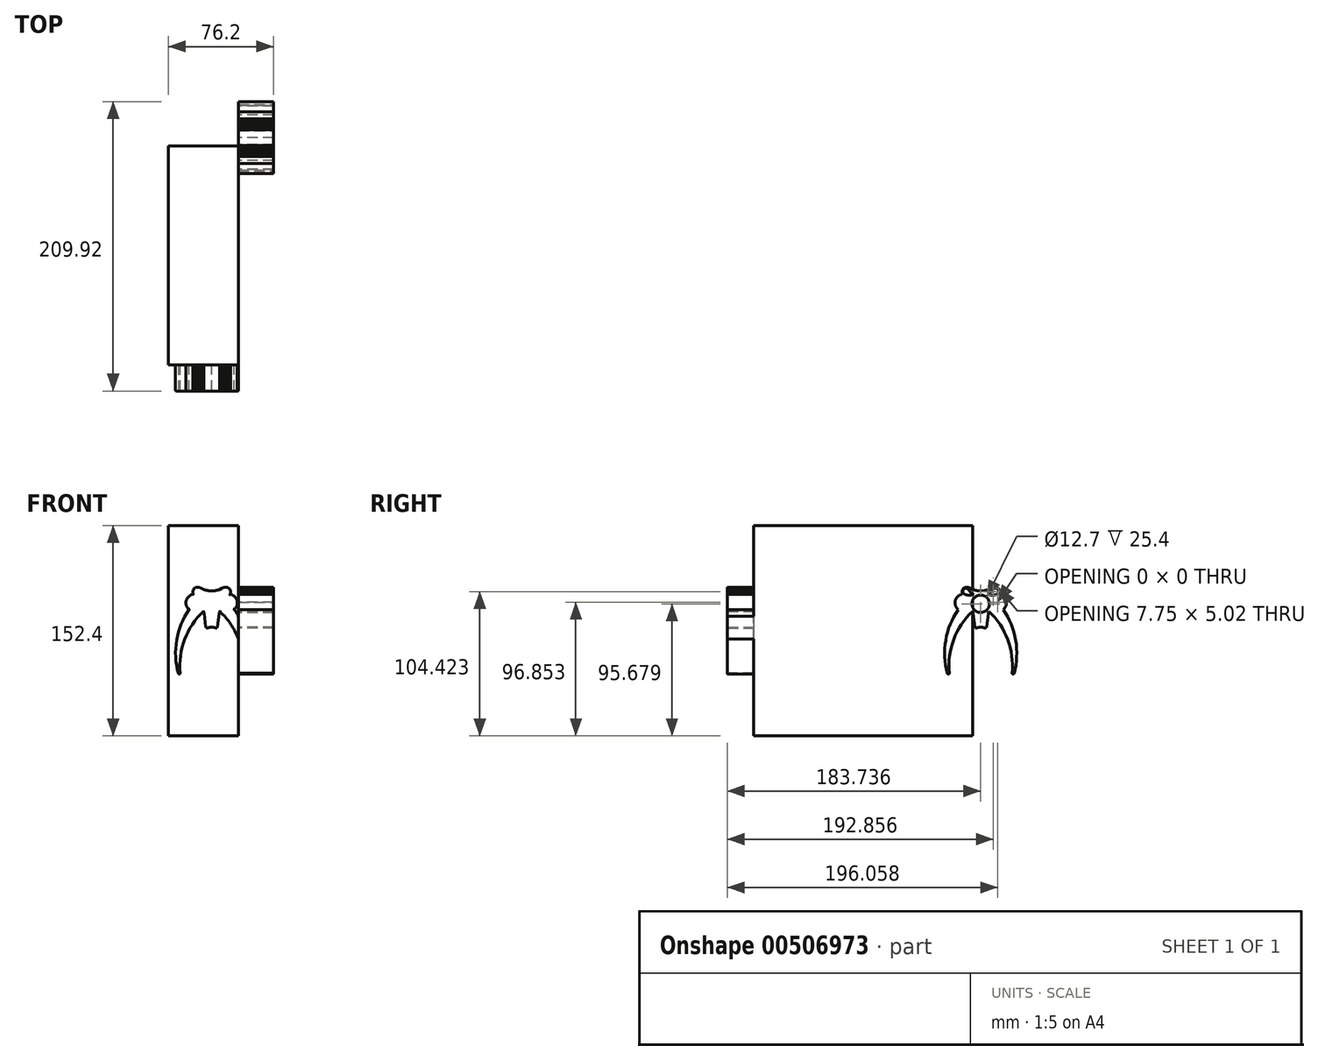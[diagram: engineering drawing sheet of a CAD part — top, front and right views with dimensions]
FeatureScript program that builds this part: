
annotation { "Feature Type Name" : "Feature", "Feature Type Description" : "" }
export const myFeature = defineFeature(function(context is Context, id is Id, definition is map)
    precondition{}
    {
        {
            var Q0;
            Q0=qCreatedBy(makeId("Front.planeOp"),FACE);
            var sketch = newSketch(context, id + "F0", { "sketchPlane" : qUnion([Q0])});
            skLineSegment(sketch, "E0.bottom", {"start": v(-25.4, 76.2) * mm, "end": v(25.4, 76.2) * mm});
            skLineSegment(sketch, "E0.top", {"start": v(-25.4, -76.2) * mm, "end": v(25.4, -76.2) * mm});
            skLineSegment(sketch, "E0.left", {"start": v(-25.4, 76.2) * mm, "end": v(-25.4, -76.2) * mm});
            skLineSegment(sketch, "E0.right", {"start": v(25.4, 76.2) * mm, "end": v(25.4, -76.2) * mm});
            skPoint(sketch, "E0.middle", {"position": v(0, 0) * mm});
            skSolve(sketch);
        }
        {
            var Q0;
            Q0 = qSketchRegion(id + "F0", true);
            extrude(context, id + "F1", {"entities" : qUnion([Q0]), "offsetDistance" : 25.4 * mm, "depth" : 152.4 * mm});
        }
        {
            var Q0;
            Q0=makeQuery(id+"F1.opExtrude","SWEPT_FACE",FACE,{"disambiguationData":[OSD([sQuery(id+"F0.wireOp",EDGE,"E0.right")])]});
            var sketch = newSketch(context, id + "F2", { "sketchPlane" : qUnion([Q0])});
            skArc(sketch, "E1", {"start": v(8.8, 2.02) * mm, "mid": v(7.41, 2.36) * mm, "end": v(5.98, 2.5) * mm});
            skLineSegment(sketch, "E2", {"start": v(11.41, 12.4) * mm, "end": v(10.25, 2.94) * mm});
            skArc(sketch, "E3", {"start": v(8.8, 2.02) * mm, "mid": v(9.74, 2.14) * mm, "end": v(10.25, 2.94) * mm});
            skArc(sketch, "E4", {"start": v(8.18, 0.06) * mm, "mid": v(10.85, 0.4) * mm, "end": v(12.3, 2.67) * mm});
            skLineSegment(sketch, "E5", {"start": v(18.57, 22.34) * mm, "end": v(19.23, 25.45) * mm});
            skLineSegment(sketch, "E6", {"start": v(19.23, 25.45) * mm, "end": v(19.56, 27.12) * mm});
            skLineSegment(sketch, "E7", {"start": v(19.56, 27.12) * mm, "end": v(19.56, 28.58) * mm});
            skLineSegment(sketch, "E8", {"start": v(19.56, 28.58) * mm, "end": v(19.23, 29.78) * mm});
            skLineSegment(sketch, "E9", {"start": v(19.23, 29.78) * mm, "end": v(18.57, 30.68) * mm});
            skLineSegment(sketch, "E10", {"start": v(18.57, 30.68) * mm, "end": v(17.62, 31.25) * mm});
            skLineSegment(sketch, "E11", {"start": v(17.62, 31.25) * mm, "end": v(16.4, 31.45) * mm});
            skLineSegment(sketch, "E12", {"start": v(16.4, 31.45) * mm, "end": v(14.98, 31.3) * mm});
            skLineSegment(sketch, "E13", {"start": v(14.98, 31.3) * mm, "end": v(13.39, 30.77) * mm});
            skLineSegment(sketch, "E14", {"start": v(13.39, 30.77) * mm, "end": v(11.7, 29.9) * mm});
            skArc(sketch, "E15", {"start": v(8.18, 0.06) * mm, "mid": v(7.1, 0.36) * mm, "end": v(5.98, 0.46) * mm});
            skArc(sketch, "E16", {"start": v(5.98, 28.72) * mm, "mid": v(8.9, 29.02) * mm, "end": v(11.7, 29.9) * mm});
            skArc(sketch, "E17", {"start": v(5.98, 28.15) * mm, "mid": v(8.97, 28.6) * mm, "end": v(11.7, 29.9) * mm});
            skArc(sketch, "E18", {"start": v(17.63, 26.41) * mm, "mid": v(18.5, 29.86) * mm, "end": v(14.95, 29.86) * mm});
            skArc(sketch, "E19", {"start": v(11.18, 26.35) * mm, "mid": v(13.29, 27.87) * mm, "end": v(14.95, 29.86) * mm});
            skArc(sketch, "E20", {"start": v(11.18, 26.35) * mm, "mid": v(14.41, 25.71) * mm, "end": v(17.63, 26.41) * mm});
            skCircle(sketch, "E21", {"center": v(8.44, 22.07) * mm, "radius": 0.52 * mm});
            skArc(sketch, "E22", {"start": v(5.98, 16.54) * mm, "mid": v(12.45, 17.6) * mm, "end": v(18.26, 20.65) * mm});
            skLineSegment(sketch, "E23", {"start": v(18.26, 20.65) * mm, "end": v(12.24, 14.18) * mm});
            skArc(sketch, "E24", {"start": v(12.24, 14.18) * mm, "mid": v(11.69, 13.36) * mm, "end": v(11.41, 12.4) * mm});
            skLineSegment(sketch, "E25", {"start": v(12.99, 8.32) * mm, "end": v(12.3, 2.69) * mm});
            skLineSegment(sketch, "E26", {"start": v(20.88, 14.44) * mm, "end": v(17.85, 13.73) * mm});
            skArc(sketch, "E27", {"start": v(20.88, 14.44) * mm, "mid": v(21.65, 14.84) * mm, "end": v(22.36, 15.36) * mm});
            skArc(sketch, "E28", {"start": v(17.85, 13.73) * mm, "mid": v(15.85, 12.88) * mm, "end": v(14.25, 11.4) * mm});
            skArc(sketch, "E29", {"start": v(5.98, 2.5) * mm, "mid": v(4.55, 2.36) * mm, "end": v(3.16, 2.02) * mm});
            skLineSegment(sketch, "E30", {"start": v(0.55, 12.4) * mm, "end": v(1.72, 2.94) * mm});
            skArc(sketch, "E31", {"start": v(1.72, 2.94) * mm, "mid": v(2.22, 2.14) * mm, "end": v(3.16, 2.02) * mm});
            skArc(sketch, "E32", {"start": v(-0.33, 2.67) * mm, "mid": v(1.11, 0.4) * mm, "end": v(3.78, 0.06) * mm});
            skLineSegment(sketch, "E33", {"start": v(0.27, 29.9) * mm, "end": v(-1.42, 30.77) * mm});
            skLineSegment(sketch, "E34", {"start": v(-1.42, 30.77) * mm, "end": v(-3.01, 31.3) * mm});
            skLineSegment(sketch, "E35", {"start": v(-3.01, 31.3) * mm, "end": v(-4.44, 31.45) * mm});
            skLineSegment(sketch, "E36", {"start": v(-4.44, 31.45) * mm, "end": v(-5.66, 31.25) * mm});
            skLineSegment(sketch, "E37", {"start": v(-5.66, 31.25) * mm, "end": v(-6.61, 30.68) * mm});
            skLineSegment(sketch, "E38", {"start": v(-6.61, 30.68) * mm, "end": v(-7.27, 29.78) * mm});
            skLineSegment(sketch, "E39", {"start": v(-7.27, 29.78) * mm, "end": v(-7.6, 28.58) * mm});
            skLineSegment(sketch, "E40", {"start": v(-7.6, 28.58) * mm, "end": v(-7.6, 27.12) * mm});
            skLineSegment(sketch, "E41", {"start": v(-7.6, 27.12) * mm, "end": v(-7.26, 25.45) * mm});
            skLineSegment(sketch, "E42", {"start": v(-7.26, 25.45) * mm, "end": v(-6.6, 22.34) * mm});
            skArc(sketch, "E43", {"start": v(5.98, 0.46) * mm, "mid": v(4.86, 0.36) * mm, "end": v(3.78, 0.06) * mm});
            skArc(sketch, "E44", {"start": v(0.27, 29.9) * mm, "mid": v(3.06, 29.02) * mm, "end": v(5.98, 28.72) * mm});
            skArc(sketch, "E45", {"start": v(0.27, 29.9) * mm, "mid": v(3, 28.6) * mm, "end": v(5.98, 28.15) * mm});
            skArc(sketch, "E46", {"start": v(-2.98, 29.86) * mm, "mid": v(-6.54, 29.86) * mm, "end": v(-5.67, 26.41) * mm});
            skArc(sketch, "E47", {"start": v(-2.98, 29.86) * mm, "mid": v(-1.32, 27.87) * mm, "end": v(0.78, 26.35) * mm});
            skArc(sketch, "E48", {"start": v(-3.55, 30.13) * mm, "mid": v(-4.98, 28.59) * mm, "end": v(-5.56, 26.57) * mm});
            skArc(sketch, "E49", {"start": v(-5.56, 26.57) * mm, "mid": v(-4.13, 28.11) * mm, "end": v(-3.55, 30.13) * mm});
            skArc(sketch, "E50", {"start": v(-5.67, 26.41) * mm, "mid": v(-2.45, 25.71) * mm, "end": v(0.78, 26.35) * mm});
            skCircle(sketch, "E51", {"center": v(3.52, 22.07) * mm, "radius": 0.52 * mm});
            skArc(sketch, "E52", {"start": v(-6.3, 20.65) * mm, "mid": v(-0.5, 17.6) * mm, "end": v(5.98, 16.54) * mm});
            skLineSegment(sketch, "E53", {"start": v(-6.3, 20.65) * mm, "end": v(-0.28, 14.18) * mm});
            skArc(sketch, "E54", {"start": v(0.55, 12.4) * mm, "mid": v(0.28, 13.36) * mm, "end": v(-0.28, 14.18) * mm});
            skLineSegment(sketch, "E55", {"start": v(-1.02, 8.32) * mm, "end": v(-0.33, 2.69) * mm});
            skArc(sketch, "E56", {"start": v(17.52, 26.57) * mm, "mid": v(16.94, 28.59) * mm, "end": v(15.51, 30.13) * mm});
            skArc(sketch, "E57", {"start": v(15.51, 30.13) * mm, "mid": v(16.1, 28.11) * mm, "end": v(17.52, 26.57) * mm});
            skArc(sketch, "E58", {"start": v(14.25, 11.4) * mm, "mid": v(13.41, 9.95) * mm, "end": v(12.99, 8.32) * mm});
            skArc(sketch, "E59", {"start": v(22.36, 15.36) * mm, "mid": v(24.4, 21.81) * mm, "end": v(19.4, 26.38) * mm});
            skLineSegment(sketch, "E60", {"start": v(-8.91, 14.44) * mm, "end": v(-5.89, 13.73) * mm});
            skArc(sketch, "E61", {"start": v(-10.4, 15.36) * mm, "mid": v(-9.68, 14.84) * mm, "end": v(-8.91, 14.44) * mm});
            skArc(sketch, "E62", {"start": v(-2.28, 11.4) * mm, "mid": v(-3.88, 12.88) * mm, "end": v(-5.89, 13.73) * mm});
            skArc(sketch, "E63", {"start": v(-1.02, 8.32) * mm, "mid": v(-1.45, 9.95) * mm, "end": v(-2.28, 11.4) * mm});
            skArc(sketch, "E64", {"start": v(-7.44, 26.38) * mm, "mid": v(-12.44, 21.81) * mm, "end": v(-10.4, 15.36) * mm});
            skCircle(sketch, "E65", {"center": v(5.94, 19.48) * mm, "radius": 3.97 * mm});
            skCircle(sketch, "E66", {"center": v(5.94, 19.48) * mm, "radius": 6.35 * mm});
            skArc(sketch, "E67", {"start": v(28.74, -30.74) * mm, "mid": v(24.77, -4.45) * mm, "end": v(8.67, 16.72) * mm});
            skArc(sketch, "E68", {"start": v(30.16, -30.97) * mm, "mid": v(30.68, -3.66) * mm, "end": v(18.26, 20.65) * mm});
            skArc(sketch, "E69", {"start": v(3.3, 16.72) * mm, "mid": v(-12.8, -4.45) * mm, "end": v(-16.78, -30.74) * mm});
            skArc(sketch, "E70", {"start": v(-6.3, 20.65) * mm, "mid": v(-18.72, -3.66) * mm, "end": v(-18.2, -30.97) * mm});
            skArc(sketch, "E71", {"start": v(28.74, -30.74) * mm, "mid": v(28.91, -31.24) * mm, "end": v(29.4, -31.44) * mm});
            skArc(sketch, "E72", {"start": v(29.4, -31.44) * mm, "mid": v(29.88, -31.35) * mm, "end": v(30.16, -30.97) * mm});
            skArc(sketch, "E73", {"start": v(-17.44, -31.44) * mm, "mid": v(-16.95, -31.24) * mm, "end": v(-16.78, -30.74) * mm});
            skArc(sketch, "E74", {"start": v(-18.2, -30.97) * mm, "mid": v(-17.91, -31.35) * mm, "end": v(-17.44, -31.44) * mm});
            skSolve(sketch);
        }
        {
            var Q0;
            Q0=makeQuery(id+"F1.opExtrude","CAP_FACE",FACE,{"disambiguationData":[OSD([sQuery(id+"F0.wireOp",EDGE,"E0.bottom"),sQuery(id+"F0.wireOp",EDGE,"E0.top"),sQuery(id+"F0.wireOp",EDGE,"E0.left"),sQuery(id+"F0.wireOp",EDGE,"E0.right")])],"isStart":false});
            var sketch = newSketch(context, id + "F3", { "sketchPlane" : qUnion([Q0])});
            skArc(sketch, "E75", {"start": v(8.8, 2.02) * mm, "mid": v(7.41, 2.36) * mm, "end": v(5.98, 2.5) * mm});
            skLineSegment(sketch, "E76", {"start": v(11.41, 12.4) * mm, "end": v(10.25, 2.94) * mm});
            skArc(sketch, "E77", {"start": v(8.8, 2.02) * mm, "mid": v(9.74, 2.14) * mm, "end": v(10.25, 2.94) * mm});
            skArc(sketch, "E78", {"start": v(8.18, 0.06) * mm, "mid": v(10.85, 0.4) * mm, "end": v(12.3, 2.67) * mm});
            skLineSegment(sketch, "E79", {"start": v(18.57, 22.34) * mm, "end": v(19.23, 25.45) * mm});
            skLineSegment(sketch, "E80", {"start": v(19.23, 25.45) * mm, "end": v(19.56, 27.12) * mm});
            skLineSegment(sketch, "E81", {"start": v(19.56, 27.12) * mm, "end": v(19.56, 28.58) * mm});
            skLineSegment(sketch, "E82", {"start": v(19.56, 28.58) * mm, "end": v(19.23, 29.78) * mm});
            skLineSegment(sketch, "E83", {"start": v(19.23, 29.78) * mm, "end": v(18.57, 30.68) * mm});
            skLineSegment(sketch, "E84", {"start": v(18.57, 30.68) * mm, "end": v(17.62, 31.25) * mm});
            skLineSegment(sketch, "E85", {"start": v(17.62, 31.25) * mm, "end": v(16.4, 31.45) * mm});
            skLineSegment(sketch, "E86", {"start": v(16.4, 31.45) * mm, "end": v(14.98, 31.3) * mm});
            skLineSegment(sketch, "E87", {"start": v(14.98, 31.3) * mm, "end": v(13.39, 30.77) * mm});
            skLineSegment(sketch, "E88", {"start": v(13.39, 30.77) * mm, "end": v(11.7, 29.9) * mm});
            skArc(sketch, "E89", {"start": v(8.18, 0.06) * mm, "mid": v(7.1, 0.36) * mm, "end": v(5.98, 0.46) * mm});
            skArc(sketch, "E90", {"start": v(5.98, 28.72) * mm, "mid": v(8.9, 29.02) * mm, "end": v(11.7, 29.9) * mm});
            skArc(sketch, "E91", {"start": v(5.98, 28.15) * mm, "mid": v(8.97, 28.6) * mm, "end": v(11.7, 29.9) * mm});
            skArc(sketch, "E92", {"start": v(17.63, 26.41) * mm, "mid": v(18.5, 29.86) * mm, "end": v(14.95, 29.86) * mm});
            skArc(sketch, "E93", {"start": v(11.18, 26.35) * mm, "mid": v(13.29, 27.87) * mm, "end": v(14.95, 29.86) * mm});
            skArc(sketch, "E94", {"start": v(11.18, 26.35) * mm, "mid": v(14.41, 25.71) * mm, "end": v(17.63, 26.41) * mm});
            skCircle(sketch, "E95", {"center": v(8.44, 22.07) * mm, "radius": 0.52 * mm});
            skArc(sketch, "E96", {"start": v(5.98, 16.54) * mm, "mid": v(12.45, 17.6) * mm, "end": v(18.26, 20.65) * mm});
            skLineSegment(sketch, "E97", {"start": v(18.26, 20.65) * mm, "end": v(12.24, 14.18) * mm});
            skArc(sketch, "E98", {"start": v(12.24, 14.18) * mm, "mid": v(11.69, 13.36) * mm, "end": v(11.41, 12.4) * mm});
            skLineSegment(sketch, "E99", {"start": v(12.99, 8.32) * mm, "end": v(12.3, 2.69) * mm});
            skLineSegment(sketch, "E100", {"start": v(20.88, 14.44) * mm, "end": v(17.85, 13.73) * mm});
            skArc(sketch, "E101", {"start": v(20.88, 14.44) * mm, "mid": v(21.65, 14.84) * mm, "end": v(22.36, 15.36) * mm});
            skArc(sketch, "E102", {"start": v(17.85, 13.73) * mm, "mid": v(15.85, 12.88) * mm, "end": v(14.25, 11.4) * mm});
            skArc(sketch, "E103", {"start": v(5.98, 2.5) * mm, "mid": v(4.55, 2.36) * mm, "end": v(3.16, 2.02) * mm});
            skLineSegment(sketch, "E104", {"start": v(0.55, 12.4) * mm, "end": v(1.72, 2.94) * mm});
            skArc(sketch, "E105", {"start": v(1.72, 2.94) * mm, "mid": v(2.22, 2.14) * mm, "end": v(3.16, 2.02) * mm});
            skArc(sketch, "E106", {"start": v(-0.33, 2.67) * mm, "mid": v(1.11, 0.4) * mm, "end": v(3.78, 0.06) * mm});
            skLineSegment(sketch, "E107", {"start": v(0.27, 29.9) * mm, "end": v(-1.42, 30.77) * mm});
            skLineSegment(sketch, "E108", {"start": v(-1.42, 30.77) * mm, "end": v(-3.01, 31.3) * mm});
            skLineSegment(sketch, "E109", {"start": v(-3.01, 31.3) * mm, "end": v(-4.44, 31.45) * mm});
            skLineSegment(sketch, "E110", {"start": v(-4.44, 31.45) * mm, "end": v(-5.66, 31.25) * mm});
            skLineSegment(sketch, "E111", {"start": v(-5.66, 31.25) * mm, "end": v(-6.61, 30.68) * mm});
            skLineSegment(sketch, "E112", {"start": v(-6.61, 30.68) * mm, "end": v(-7.27, 29.78) * mm});
            skLineSegment(sketch, "E113", {"start": v(-7.27, 29.78) * mm, "end": v(-7.6, 28.58) * mm});
            skLineSegment(sketch, "E114", {"start": v(-7.6, 28.58) * mm, "end": v(-7.6, 27.12) * mm});
            skLineSegment(sketch, "E115", {"start": v(-7.6, 27.12) * mm, "end": v(-7.26, 25.45) * mm});
            skLineSegment(sketch, "E116", {"start": v(-7.26, 25.45) * mm, "end": v(-6.6, 22.34) * mm});
            skArc(sketch, "E117", {"start": v(5.98, 0.46) * mm, "mid": v(4.86, 0.36) * mm, "end": v(3.78, 0.06) * mm});
            skArc(sketch, "E118", {"start": v(0.27, 29.9) * mm, "mid": v(3.06, 29.02) * mm, "end": v(5.98, 28.72) * mm});
            skArc(sketch, "E119", {"start": v(0.27, 29.9) * mm, "mid": v(3, 28.6) * mm, "end": v(5.98, 28.15) * mm});
            skArc(sketch, "E120", {"start": v(-2.98, 29.86) * mm, "mid": v(-6.54, 29.86) * mm, "end": v(-5.67, 26.41) * mm});
            skArc(sketch, "E121", {"start": v(-2.98, 29.86) * mm, "mid": v(-1.32, 27.87) * mm, "end": v(0.78, 26.35) * mm});
            skArc(sketch, "E122", {"start": v(-3.55, 30.13) * mm, "mid": v(-4.98, 28.59) * mm, "end": v(-5.56, 26.57) * mm});
            skArc(sketch, "E123", {"start": v(-5.56, 26.57) * mm, "mid": v(-4.13, 28.11) * mm, "end": v(-3.55, 30.13) * mm});
            skArc(sketch, "E124", {"start": v(-5.67, 26.41) * mm, "mid": v(-2.45, 25.71) * mm, "end": v(0.78, 26.35) * mm});
            skCircle(sketch, "E125", {"center": v(3.52, 22.07) * mm, "radius": 0.52 * mm});
            skArc(sketch, "E126", {"start": v(-6.3, 20.65) * mm, "mid": v(-0.5, 17.6) * mm, "end": v(5.98, 16.54) * mm});
            skLineSegment(sketch, "E127", {"start": v(-6.3, 20.65) * mm, "end": v(-0.28, 14.18) * mm});
            skArc(sketch, "E128", {"start": v(0.55, 12.4) * mm, "mid": v(0.28, 13.36) * mm, "end": v(-0.28, 14.18) * mm});
            skLineSegment(sketch, "E129", {"start": v(-1.02, 8.32) * mm, "end": v(-0.33, 2.69) * mm});
            skArc(sketch, "E130", {"start": v(17.52, 26.57) * mm, "mid": v(16.94, 28.59) * mm, "end": v(15.51, 30.13) * mm});
            skArc(sketch, "E131", {"start": v(15.51, 30.13) * mm, "mid": v(16.1, 28.11) * mm, "end": v(17.52, 26.57) * mm});
            skArc(sketch, "E132", {"start": v(14.25, 11.4) * mm, "mid": v(13.41, 9.95) * mm, "end": v(12.99, 8.32) * mm});
            skArc(sketch, "E133", {"start": v(22.36, 15.36) * mm, "mid": v(24.4, 21.81) * mm, "end": v(19.4, 26.38) * mm});
            skLineSegment(sketch, "E134", {"start": v(-8.91, 14.44) * mm, "end": v(-5.89, 13.73) * mm});
            skArc(sketch, "E135", {"start": v(-10.4, 15.36) * mm, "mid": v(-9.68, 14.84) * mm, "end": v(-8.91, 14.44) * mm});
            skArc(sketch, "E136", {"start": v(-2.28, 11.4) * mm, "mid": v(-3.88, 12.88) * mm, "end": v(-5.89, 13.73) * mm});
            skArc(sketch, "E137", {"start": v(-1.02, 8.32) * mm, "mid": v(-1.45, 9.95) * mm, "end": v(-2.28, 11.4) * mm});
            skArc(sketch, "E138", {"start": v(-7.44, 26.38) * mm, "mid": v(-12.44, 21.81) * mm, "end": v(-10.4, 15.36) * mm});
            skCircle(sketch, "E139", {"center": v(5.94, 19.48) * mm, "radius": 3.97 * mm});
            skCircle(sketch, "E140", {"center": v(5.94, 19.48) * mm, "radius": 6.35 * mm});
            skArc(sketch, "E141", {"start": v(28.74, -30.74) * mm, "mid": v(24.77, -4.45) * mm, "end": v(8.67, 16.72) * mm});
            skArc(sketch, "E142", {"start": v(30.16, -30.97) * mm, "mid": v(30.68, -3.66) * mm, "end": v(18.26, 20.65) * mm});
            skArc(sketch, "E143", {"start": v(3.3, 16.72) * mm, "mid": v(-12.8, -4.45) * mm, "end": v(-16.78, -30.74) * mm});
            skArc(sketch, "E144", {"start": v(-6.3, 20.65) * mm, "mid": v(-18.72, -3.66) * mm, "end": v(-18.2, -30.97) * mm});
            skArc(sketch, "E145", {"start": v(28.74, -30.74) * mm, "mid": v(28.91, -31.24) * mm, "end": v(29.4, -31.44) * mm});
            skArc(sketch, "E146", {"start": v(29.4, -31.44) * mm, "mid": v(29.88, -31.35) * mm, "end": v(30.16, -30.97) * mm});
            skArc(sketch, "E147", {"start": v(-17.44, -31.44) * mm, "mid": v(-16.95, -31.24) * mm, "end": v(-16.78, -30.74) * mm});
            skArc(sketch, "E148", {"start": v(-18.2, -30.97) * mm, "mid": v(-17.91, -31.35) * mm, "end": v(-17.44, -31.44) * mm});
            skSolve(sketch);
        }
        {
            var Q0;
            Q0=makeQuery(id+"F3.imprint","IMPRINT",FACE,{"disambiguationData":[TD([[makeQuery(id+"F3.imprint","IMPRINT",EDGE,{"derivedFrom":sQuery(id+"F3.wireOp",EDGE,"E75")}),1.0]])]});
            extrude(context, id + "F4", {"entities" : qUnion([Q0]), "operationType" : NewBodyOperationType.ADD, "depth" : 6.35 * mm, "offsetDistance" : 25.4 * mm});
        }
        {
            var Q0;
            Q0=makeQuery(id+"F3.imprint","IMPRINT",FACE,{"disambiguationData":[TD([[makeQuery(id+"F3.imprint","IMPRINT",EDGE,{"derivedFrom":sQuery(id+"F3.wireOp",EDGE,"E90")}),-1.0]])]});
            var Q1;
            {var subQ4=sQuery(id+"F3.wireOp",EDGE,"E100");Q1=makeQuery(id+"F3.imprint","IMPRINT",FACE,{"disambiguationData":[TD([[makeQuery(id+"F3.imprint","IMPRINT",EDGE,{"derivedFrom":subQ4}),1.0]])]});}
            var Q2;
            {var subQ5=sQuery(id+"F3.wireOp",EDGE,"E134");Q2=makeQuery(id+"F3.imprint","IMPRINT",FACE,{"disambiguationData":[TD([[makeQuery(id+"F3.imprint","IMPRINT",EDGE,{"derivedFrom":subQ5}),-1.0]])]});}
            var Q3;
            {var subQ1=sQuery(id+"F3.wireOp",EDGE,"E127");Q3=makeQuery(id+"F3.imprint","IMPRINT",FACE,{"disambiguationData":[TD([[makeQuery(id+"F3.imprint","IMPRINT",EDGE,{"derivedFrom":subQ1}),1.0]])]});}
            var Q4;
            Q4=makeQuery(id+"F3.imprint","IMPRINT",FACE,{"disambiguationData":[TD([[makeQuery(id+"F3.imprint","IMPRINT",EDGE,{"derivedFrom":sQuery(id+"F3.wireOp",EDGE,"E75")}),-1.0]])]});
            var Q5;
            {var subQ1=sQuery(id+"F3.wireOp",EDGE,"E100");Q5=makeQuery(id+"F3.imprint","IMPRINT",FACE,{"disambiguationData":[TD([[makeQuery(id+"F3.imprint","IMPRINT",EDGE,{"derivedFrom":subQ1}),-1.0]])]});}
            var Q6;
            {var subQ1=sQuery(id+"F3.wireOp",EDGE,"E96");var subQ5=sQuery(id+"F3.wireOp",EDGE,"E142");var subQ6=makeQuery(id+"F3.imprint","INTERSECT",VERTEX,{"derivedFrom":[subQ1,subQ5]});Q6=makeQuery(id+"F3.imprint","IMPRINT",FACE,{"disambiguationData":[TD([[makeQuery(id+"F3.imprint","IMPRINT",EDGE,{"disambiguationData":[TD([[subQ6,1.0]])],"derivedFrom":subQ1}),-1.0]])]});}
            var Q7;
            {var subQ18=sQuery(id+"F3.wireOp",EDGE,"E81");Q7=makeQuery(id+"F3.imprint","IMPRINT",FACE,{"disambiguationData":[TD([[makeQuery(id+"F3.imprint","IMPRINT",EDGE,{"derivedFrom":subQ18}),1.0]])]});}
            var Q8;
            {var subQ2=sQuery(id+"F3.wireOp",EDGE,"E139");var subQ4=sQuery(id+"F3.wireOp",EDGE,"E95");var subQ11=makeQuery(id+"F3.imprint","INTERSECT",VERTEX,{"disambiguationData":[OD(0.0)],"derivedFrom":[subQ4,subQ2]});Q8=makeQuery(id+"F3.imprint","IMPRINT",FACE,{"disambiguationData":[TD([[makeQuery(id+"F3.imprint","IMPRINT",EDGE,{"disambiguationData":[TD([[subQ11,1.0]])],"derivedFrom":subQ4}),1.0]])]});}
            var Q9;
            Q9=makeQuery(id+"F1.opExtrude","CAP_FACE",FACE,{"disambiguationData":[OSD([sQuery(id+"F0.wireOp",EDGE,"E0.bottom"),sQuery(id+"F0.wireOp",EDGE,"E0.top"),sQuery(id+"F0.wireOp",EDGE,"E0.left"),sQuery(id+"F0.wireOp",EDGE,"E0.right")])],"isStart":false});
            var Q10;
            Q10=makeQuery(id+"F1.opExtrude","CAP_FACE",FACE,{"disambiguationData":[OSD([sQuery(id+"F0.wireOp",EDGE,"E0.bottom"),sQuery(id+"F0.wireOp",EDGE,"E0.top"),sQuery(id+"F0.wireOp",EDGE,"E0.left"),sQuery(id+"F0.wireOp",EDGE,"E0.right")])],"isStart":true});
            var Q11;
            Q11=makeQuery(id+"F3.imprint","IMPRINT",FACE,{"disambiguationData":[TD([[makeQuery(id+"F3.imprint","IMPRINT",EDGE,{"derivedFrom":sQuery(id+"F3.wireOp",EDGE,"E120")}),1.0]])]});
            var Q12;
            Q12=makeQuery(id+"F3.imprint","IMPRINT",FACE,{"disambiguationData":[TD([[makeQuery(id+"F3.imprint","IMPRINT",EDGE,{"derivedFrom":sQuery(id+"F3.wireOp",EDGE,"E92")}),1.0]])]});
            extrude(context, id + "F5", {"entities" : qUnion([Q0, Q1, Q2, Q3, Q4, Q5, Q6, Q7, Q8, Q9, Q10, Q11, Q12]), "operationType" : NewBodyOperationType.ADD, "depth" : 25.4 * mm, "offsetDistance" : 25.4 * mm});
        }
        {
            var Q0;
            {var subQ0=sQuery(id+"F0.wireOp",EDGE,"E0.right");var subQ1=sQuery(id+"F0.wireOp",EDGE,"E0.left");var subQ2=sQuery(id+"F0.wireOp",EDGE,"E0.top");var subQ3=sQuery(id+"F0.wireOp",EDGE,"E0.bottom");var subQ4=sQuery(id+"F3.wireOp",EDGE,"E96");Q0=makeQuery(id+"F5.boolean.opBoolean","MERGE",FACE,{"derivedFrom":[makeQuery(id+"F5.opExtrude","CAP_FACE",FACE,{"disambiguationData":[OSD([sQuery(id+"F3.wireOp",EDGE,"E75"),sQuery(id+"F3.wireOp",EDGE,"E76"),sQuery(id+"F3.wireOp",EDGE,"E77"),sQuery(id+"F3.wireOp",EDGE,"E80"),sQuery(id+"F3.wireOp",EDGE,"E81"),sQuery(id+"F3.wireOp",EDGE,"E82"),sQuery(id+"F3.wireOp",EDGE,"E83"),sQuery(id+"F3.wireOp",EDGE,"E84"),sQuery(id+"F3.wireOp",EDGE,"E85"),sQuery(id+"F3.wireOp",EDGE,"E86"),sQuery(id+"F3.wireOp",EDGE,"E87"),sQuery(id+"F3.wireOp",EDGE,"E88"),sQuery(id+"F3.wireOp",EDGE,"E90"),subQ4,sQuery(id+"F3.wireOp",EDGE,"E97"),sQuery(id+"F3.wireOp",EDGE,"E98"),sQuery(id+"F3.wireOp",EDGE,"E101"),sQuery(id+"F3.wireOp",EDGE,"E103"),sQuery(id+"F3.wireOp",EDGE,"E104"),sQuery(id+"F3.wireOp",EDGE,"E105"),sQuery(id+"F3.wireOp",EDGE,"E107"),sQuery(id+"F3.wireOp",EDGE,"E108"),sQuery(id+"F3.wireOp",EDGE,"E109"),sQuery(id+"F3.wireOp",EDGE,"E110"),sQuery(id+"F3.wireOp",EDGE,"E111"),sQuery(id+"F3.wireOp",EDGE,"E112"),sQuery(id+"F3.wireOp",EDGE,"E113"),sQuery(id+"F3.wireOp",EDGE,"E114"),sQuery(id+"F3.wireOp",EDGE,"E115"),sQuery(id+"F3.wireOp",EDGE,"E118"),sQuery(id+"F3.wireOp",EDGE,"E122"),sQuery(id+"F3.wireOp",EDGE,"E123"),sQuery(id+"F3.wireOp",EDGE,"E128"),sQuery(id+"F3.wireOp",EDGE,"E130"),sQuery(id+"F3.wireOp",EDGE,"E131"),sQuery(id+"F3.wireOp",EDGE,"E133"),sQuery(id+"F3.wireOp",EDGE,"E138"),sQuery(id+"F3.wireOp",EDGE,"E140"),sQuery(id+"F3.wireOp",EDGE,"E141"),sQuery(id+"F3.wireOp",EDGE,"E142"),sQuery(id+"F3.wireOp",EDGE,"E143"),sQuery(id+"F3.wireOp",EDGE,"E144"),sQuery(id+"F3.wireOp",EDGE,"E145"),sQuery(id+"F3.wireOp",EDGE,"E146"),sQuery(id+"F3.wireOp",EDGE,"E147"),sQuery(id+"F3.wireOp",EDGE,"E148")])],"isStart":false}),makeQuery(id+"F5.opExtrude","CAP_FACE",FACE,{"disambiguationData":[OSD([sQuery(id+"F3.wireOp",EDGE,"E95"),subQ4,sQuery(id+"F3.wireOp",EDGE,"E125"),sQuery(id+"F3.wireOp",EDGE,"E126"),sQuery(id+"F3.wireOp",EDGE,"E139")])],"isStart":false}),makeQuery(id+"F5.opExtrude","CAP_FACE",FACE,{"disambiguationData":[OSD([subQ3,subQ2,subQ1,subQ0]),TDD([makeQuery(id+"F1.opExtrude","CAP_FACE",FACE,{"disambiguationData":[OSD([subQ3,subQ2,subQ1,subQ0])],"isStart":false})])],"isStart":false})]});}
            fillet(context, id + "F6", {"entities" : qUnion([Q0]), "radius" : 0.5 * mm, "tangentPropagation" : true, "allowEdgeOverflow" : false});
        }
        {
            var Q0;
            Q0 = qSketchRegion(id + "F2", true);
            extrude(context, id + "F7", {"entities" : qUnion([Q0]), "operationType" : NewBodyOperationType.ADD, "depth" : 25.4 * mm, "offsetDistance" : 25.4 * mm});
        }
    });
